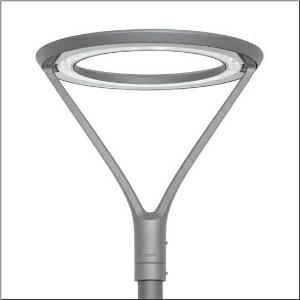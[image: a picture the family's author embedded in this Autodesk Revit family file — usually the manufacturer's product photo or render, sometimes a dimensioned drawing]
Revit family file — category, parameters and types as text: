
# Revit family: dl_r__20___p1_0a_5xa51283wr008p_ca28
name_source: partatom
category: Lighting Fixtures
units: mm (PartAtom-declared; Revit-internal decimal feet)

## family parameters
Cut with Voids When Loaded = No
Host = Face
Light Source = No
Part Type = Normal
Room Calculation Point = No
Round Connector Dimension = Use Diameter
Shared = No

## types (1)
- --- (1 x LED, 4220 lm, 34.3 W, 3000K)
    Apparent Load = 34 VA
    CIE Flux Codes = 31 71 96 100 100
    Color Rendering = 70
    Color Temperature = 3000K
    Default Elevation = 1800 mm
    Description = DL® 20, mast luminaire, primary light control with cycle path optic, highly specular, primary optical cover: cover, of toughened safety glass of clear glass with excellent transmission level, light distribution: P1.0a, light emission: direct distribution, primary light characteristic: asymmetric, installation type: post-top, LED, High Power LED, rated luminous flux: 4.240lm, luminous efficacy: 81lm/W, light colour: 730, colour temperature: 3000K, control gear: Plus, control: overheat protection, power reduction, digital communication interface, constant luminous flux control, time-dependent luminous flux control, flexible luminous flux parameterisation, electronic power reduction, mains connection: 230..240V, 50/60Hz, connection cable pre-assembled, cable length: 5m, start of lifetime: 53W, end of service life: 54W, reduction: 24W, luminaire housing, upper part, of cast aluminium, powder-coated, Siteco® metallic grey (DB 702S), diameter: 690mm, height: 690mm, spigot size: 76mm (post-top), mounting height: 4..6m, luminaire housing, of cast aluminium, powder-coated, Siteco® metallic grey (DB 702S), equipment: Power, protection rating (complete): IP66, insulation class (complete): insulation class II (safety insulation), certification: CE, ENEC, VDE, impact resistance: IK08, permissible operating ambient temperature: -25..+30°C, standard-compliant lighting for roads and squares, packaging unit: 1 piece

Light Distribution: P1.0a
    Height = 690 mm
    Lamp = 1 x LED
    Lamp Light Flux = 4220 lm
    Lamp Power = 34.3 W
    Lamp count = 1
    Length = 690 mm
    Luminous efficacy = 123 lm/W
    Manufacturer = Siteco
    ModVariant = No
    Model = 5XA51283WR008P
    Number of Poles = 1
    OnlyDefault = Yes
    Power Factor = 1
    Product Name = DL® 20 | P1.0a
    Product group = mast luminaire | pylon top
    ProductGroupID = 6100
    Protection Class = Protection class II
    Protection Degree = IP 66
    RLX_Detail_Level = 1
    RLX_Emergency_Light_Flux = 0 lm
    RLX_Emergency_Type = 0
    RLX_Emergency_Type_DB = No
    RlxData = <blob elided: 206837 chars, md5=3e074a9a>
    Socket = socket
    Standby Power = 0 W
    System Light Flux = 4220 lm
    System Power = 34 W
    Type Comments = factory setting: luminous flux: 100 % | dim-lin: 254 | 464 mA
    Type Image = l_1006001.jpg
    URL = http://relux.com
    VarID = @adj_077162
    Voltage = 0 V
    Weight = 0.00 kg
    Width = 0 mm  [stored 0 ft]

note: [stored X ft] marks values corroborated as IEEE doubles in the binary element streams (Revit-internal decimal feet)

## geometry (parser evidence)
native form markers: Blend x4, Sweep x10
no freeform markers — native parametric forms only
